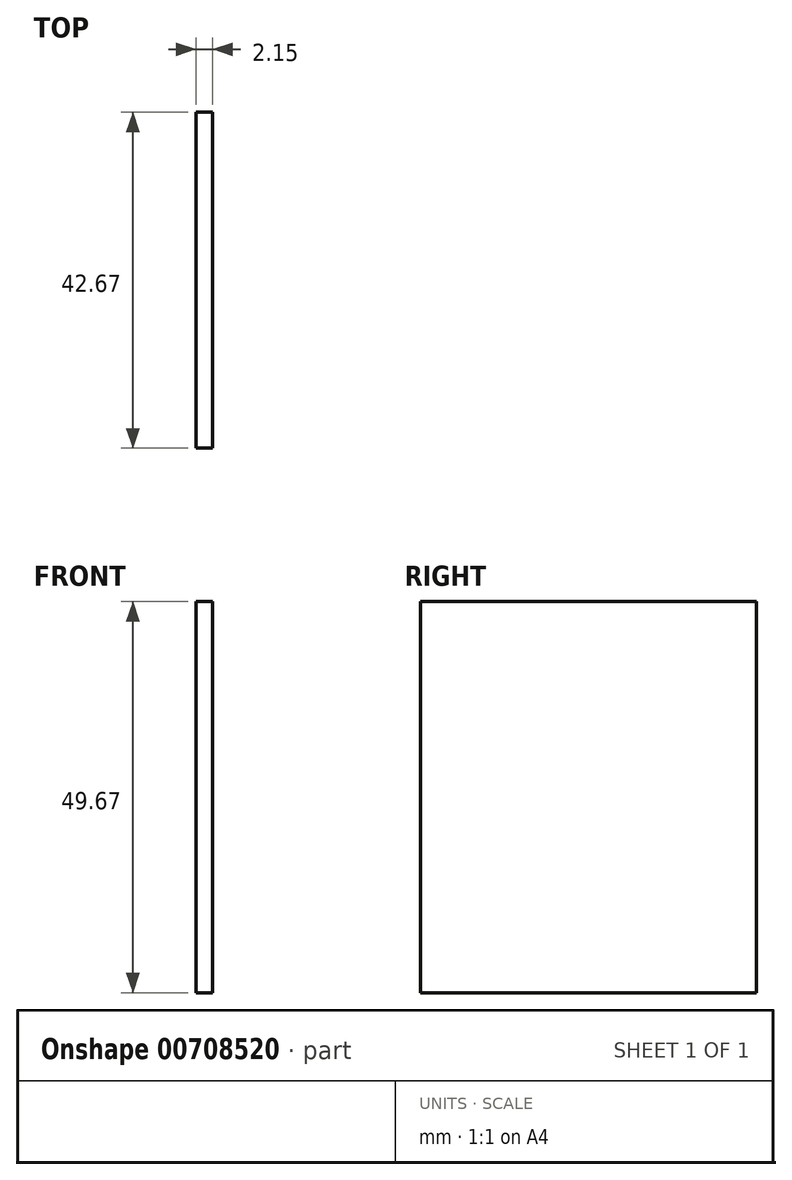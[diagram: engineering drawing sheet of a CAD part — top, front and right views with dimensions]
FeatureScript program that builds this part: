
annotation { "Feature Type Name" : "Feature", "Feature Type Description" : "" }
export const myFeature = defineFeature(function(context is Context, id is Id, definition is map)
    precondition{}
    {
        {
            var Q0;
            Q0=qCreatedBy(makeId("Front.planeOp"),FACE);
            var sketch = newSketch(context, id + "F0", { "sketchPlane" : qUnion([Q0])});
            skLineSegment(sketch, "E0.bottom", {"start": v(-13.3, 13.83) * mm, "end": v(-11.14, 13.83) * mm});
            skLineSegment(sketch, "E0.top", {"start": v(-13.3, -35.84) * mm, "end": v(-11.14, -35.84) * mm});
            skLineSegment(sketch, "E0.left", {"start": v(-13.3, 13.83) * mm, "end": v(-13.3, -35.84) * mm});
            skLineSegment(sketch, "E0.right", {"start": v(-11.14, 13.83) * mm, "end": v(-11.14, -35.84) * mm});
            skSolve(sketch);
        }
        {
            var Q0;
            Q0=makeQuery(id+"F0.imprint","IMPRINT",FACE,{"disambiguationData":[TD([[makeQuery(id+"F0.imprint","IMPRINT",EDGE,{"derivedFrom":sQuery(id+"F0.wireOp",EDGE,"E0.bottom")}),-1.0]])]});
            extrude(context, id + "F1", {"entities" : qUnion([Q0]), "depth" : 42.67 * mm, "offsetDistance" : 25.4 * mm});
        }
    });
